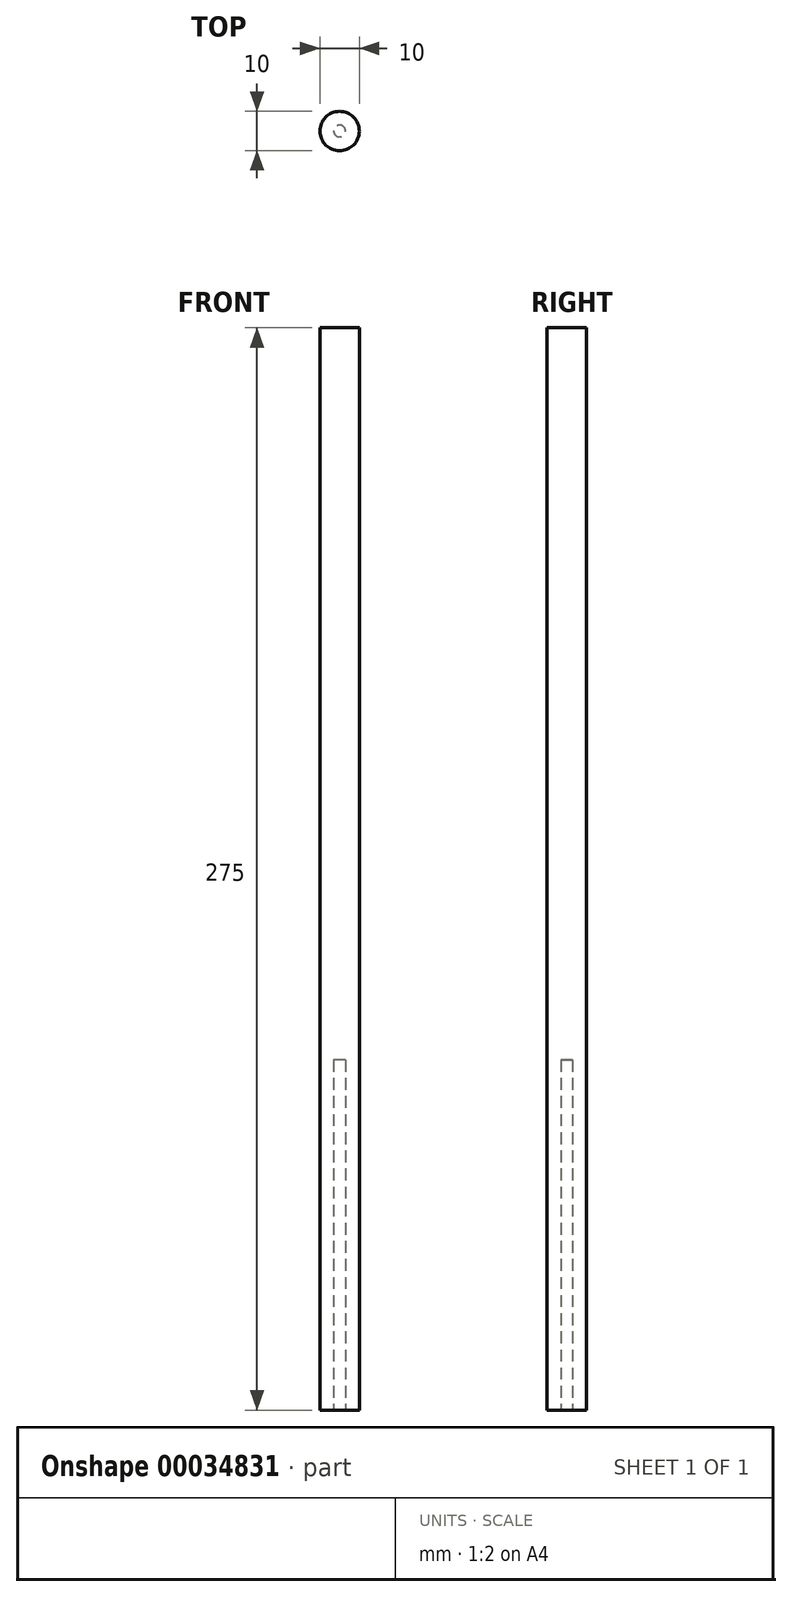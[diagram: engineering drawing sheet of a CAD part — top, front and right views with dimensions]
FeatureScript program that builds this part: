
annotation { "Feature Type Name" : "Feature", "Feature Type Description" : "" }
export const myFeature = defineFeature(function(context is Context, id is Id, definition is map)
    precondition{}
    {
        {
            var Q0;
            Q0=qCreatedBy(makeId("Top.planeOp"),FACE);
            var sketch = newSketch(context, id + "F0", { "sketchPlane" : qUnion([Q0])});
            skCircle(sketch, "E0", {"center": v(0, 0) * mm, "radius": 5 * mm});
            skSolve(sketch);
        }
        {
            var Q0;
            Q0 = qSketchRegion(id + "F0", true);
            extrude(context, id + "F1", {"entities" : qUnion([Q0]), "flatOperationType" : FlatOperationType.REMOVE, "offsetDistance" : 25 * mm, "depth" : 275 * mm, "domain" : OperationDomain.MODEL});
        }
        {
            var Q0;
            Q0=qCreatedBy(makeId("Top.planeOp"),FACE);
            var sketch = newSketch(context, id + "F2", { "sketchPlane" : qUnion([Q0])});
            skCircle(sketch, "E1", {"center": v(0, 0) * mm, "radius": 1.5 * mm});
            skSolve(sketch);
        }
        {
            var Q0;
            Q0 = qSketchRegion(id + "F2", true);
            extrude(context, id + "F3", {"entities" : qUnion([Q0]), "depth" : 89 * mm});
        }
    });
